# Revit family: HBL
name_source: partatom
category: Lighting Fixtures
units: mm (PartAtom-declared; Revit-internal decimal feet)

## family parameters
Cut with Voids When Loaded = No
Host = Face
Light Source = No
OmniClass Number = 23.80.70.14.14
OmniClass Title = Exterior Floodlights
Part Type = Normal
Room Calculation Point = No
Round Connector Dimension = Use Diameter
Shared = No

## types (3) — shared parameters
Apparent Load = 0 VA
Default Elevation = 48.000"
Description = The Current LED Highbay is designed to efficiently light any
large interior space such as heavy industrial settings, warehouses,
gyms, churches, swimming pools/natatorium and shopping malls
Lens = White Glass
Manufacturer = Columbia Lighting
Model = Heavy industrial, cast aluminum LED Highbay
Photometrics = Web HBL : HBL-48LU-5K-A-070
URL = https://www.currentlighting.com

## per-type parameters (varying)
| type | Finish | Lamp | Total Input Wattage | Voltage |
| HBL - BL | Black | LED |  |  |
| HBL - WH | White |  | 112 - 169W | 120 - 277V |
| HBL - GR | Gray |  |  |  |

## geometry (parser evidence)
native form markers: Blend x6, Sweep x10
no freeform markers — native parametric forms only
